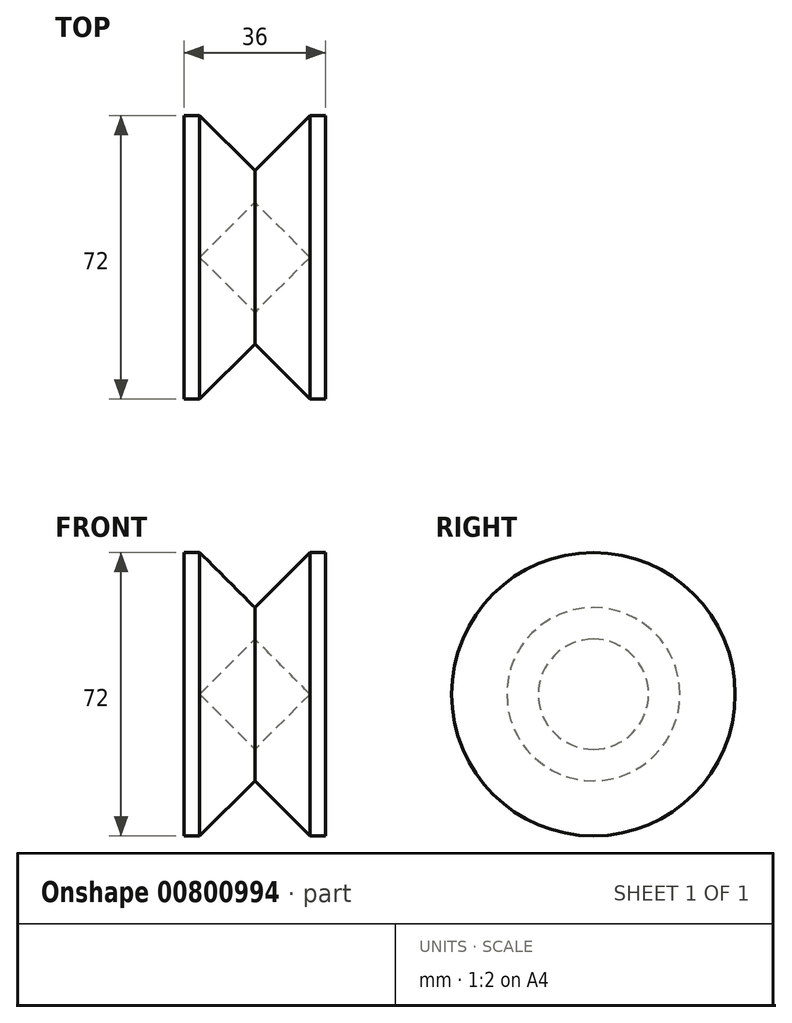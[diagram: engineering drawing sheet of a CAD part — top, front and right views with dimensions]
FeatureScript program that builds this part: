
annotation { "Feature Type Name" : "Feature", "Feature Type Description" : "" }
export const myFeature = defineFeature(function(context is Context, id is Id, definition is map)
    precondition{}
    {
        {
            var Q0;
            Q0=qCreatedBy(makeId("Top.planeOp"),FACE);
            var sketch = newSketch(context, id + "F0", { "sketchPlane" : qUnion([Q0])});
            skLineSegment(sketch, "E0", {"start": v(0, 0) * mm, "end": v(0, -36) * mm});
            skLineSegment(sketch, "E1", {"start": v(0, -36) * mm, "end": v(4, -36) * mm});
            skLineSegment(sketch, "E2", {"start": v(4, -36) * mm, "end": v(18, -22) * mm});
            skLineSegment(sketch, "E3", {"start": v(18, -22) * mm, "end": v(32, -36) * mm});
            skLineSegment(sketch, "E4", {"start": v(32, -36) * mm, "end": v(36, -36) * mm});
            skLineSegment(sketch, "E5", {"start": v(36, -36) * mm, "end": v(36, 0) * mm});
            skLineSegment(sketch, "E6", {"start": v(36, 0) * mm, "end": v(32, 0) * mm});
            skLineSegment(sketch, "E7", {"start": v(32, 0) * mm, "end": v(18, -14) * mm});
            skLineSegment(sketch, "E8", {"start": v(18, -14) * mm, "end": v(4, 0) * mm});
            skLineSegment(sketch, "E9", {"start": v(4, 0) * mm, "end": v(0, 0) * mm});
            skLineSegment(sketch, "E10", {"start": v(4, -30.34) * mm, "end": v(16.34, -18) * mm});
            skLineSegment(sketch, "E11", {"start": v(16.34, -18) * mm, "end": v(4, -5.66) * mm});
            skLineSegment(sketch, "E12", {"start": v(4, -5.66) * mm, "end": v(4, -30.34) * mm});
            skLineSegment(sketch, "E13", {"start": v(18, -14) * mm, "end": v(18, -22) * mm, "construction": true});
            skLineSegment(sketch, "E14.MirrorCS", {"start": v(19.66, -18) * mm, "end": v(32, -5.66) * mm});
            skLineSegment(sketch, "E15.MirrorCS", {"start": v(32, -5.66) * mm, "end": v(32, -30.34) * mm});
            skLineSegment(sketch, "E16.MirrorCS", {"start": v(32, -30.34) * mm, "end": v(19.66, -18) * mm});
            skLineSegment(sketch, "E17", {"start": v(0, 0) * mm, "end": v(36, 0) * mm, "construction": true});
            skSolve(sketch);
        }
        {
            var Q0;
            Q0=makeQuery(id+"F0.imprint","IMPRINT",FACE,{"disambiguationData":[TD([[makeQuery(id+"F0.imprint","IMPRINT",EDGE,{"derivedFrom":sQuery(id+"F0.wireOp",EDGE,"E10")}),1.0]])]});
            var Q1;
            Q1=makeQuery(id+"F0.imprint","IMPRINT",FACE,{"disambiguationData":[TD([[makeQuery(id+"F0.imprint","IMPRINT",EDGE,{"derivedFrom":sQuery(id+"F0.wireOp",EDGE,"E0")}),1.0]])]});
            var Q2;
            Q2=makeQuery(id+"F0.imprint","IMPRINT",FACE,{"disambiguationData":[TD([[makeQuery(id+"F0.imprint","IMPRINT",EDGE,{"derivedFrom":sQuery(id+"F0.wireOp",EDGE,"E14.MirrorCS")}),-1.0]])]});
            var Q3;
            Q3=sQuery(id+"F0.wireOp",EDGE,"E17");
            revolve(context, id + "F1", {"surfaceOperationType" : NewSurfaceOperationType.NEW, "entities" : qUnion([Q0, Q1, Q2]), "axis" : qUnion([Q3]), "revolveType" : RevolveType.FULL});
        }
    });
